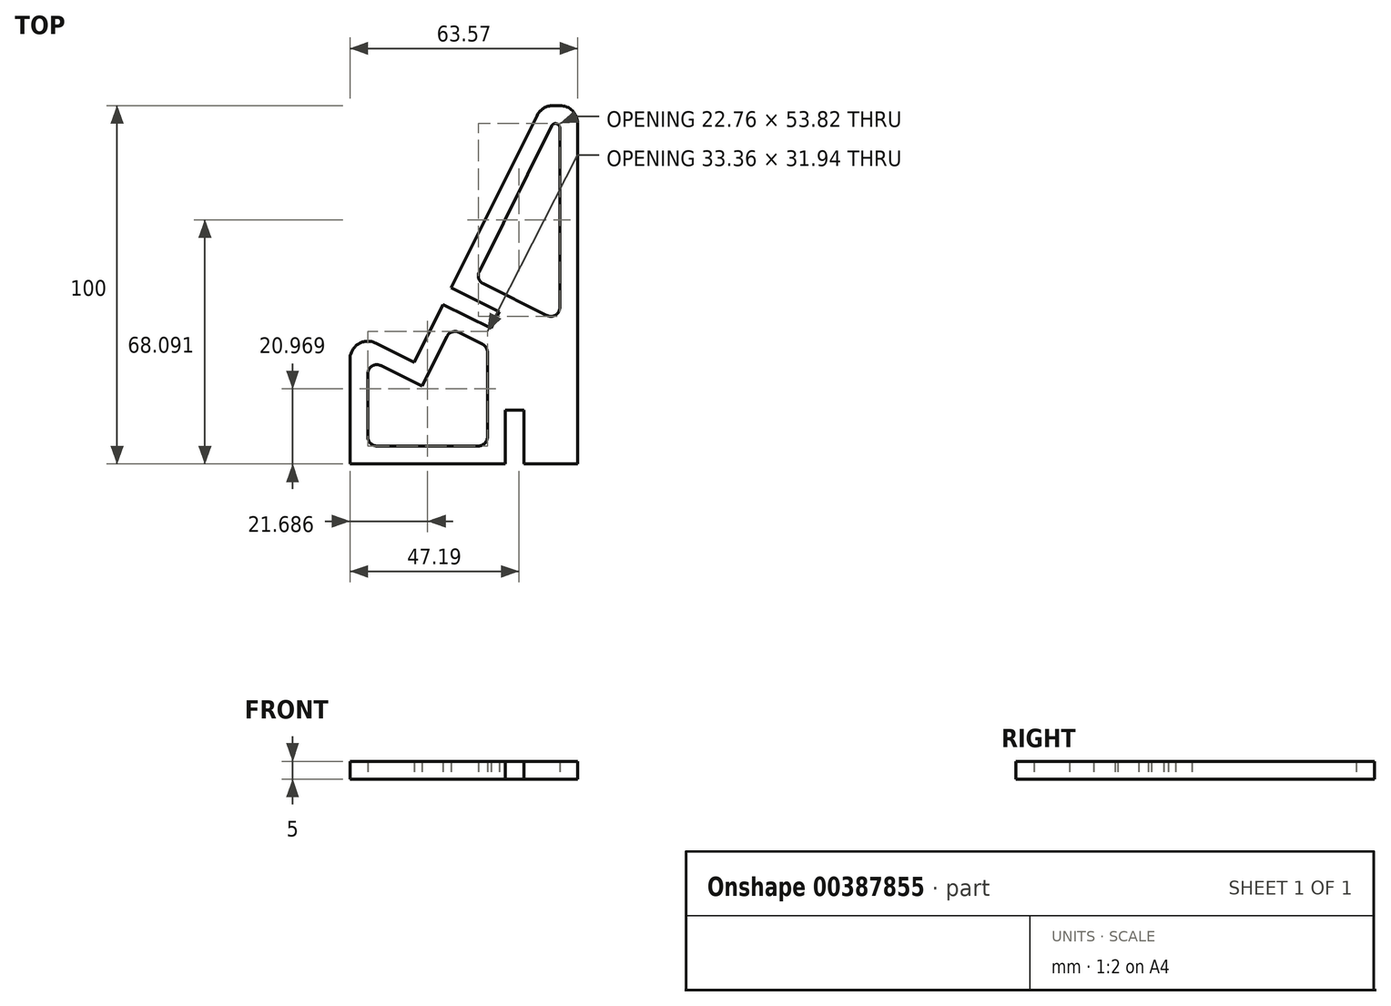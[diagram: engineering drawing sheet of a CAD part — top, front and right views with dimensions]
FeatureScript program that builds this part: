
annotation { "Feature Type Name" : "Feature", "Feature Type Description" : "" }
export const myFeature = defineFeature(function(context is Context, id is Id, definition is map)
    precondition{}
    {
        {
            var Q0;
            Q0=qCreatedBy(makeId("Top.planeOp"),FACE);
            var sketch = newSketch(context, id + "F0", { "sketchPlane" : qUnion([Q0])});
            skLineSegment(sketch, "E0", {"start": v(28.14, 25.7) * mm, "end": v(28.14, -69.3) * mm});
            skLineSegment(sketch, "E1", {"start": v(23.14, 30.7) * mm, "end": v(21.23, 30.7) * mm});
            skLineSegment(sketch, "E2", {"start": v(16.76, 27.94) * mm, "end": v(-7.18, -20.13) * mm});
            skLineSegment(sketch, "E3", {"start": v(-17.52, -40.9) * mm, "end": v(-28.2, -35.59) * mm});
            skLineSegment(sketch, "E4", {"start": v(-35.43, -40.06) * mm, "end": v(-35.43, -69.3) * mm});
            skLineSegment(sketch, "E5", {"start": v(7.94, -69.3) * mm, "end": v(7.94, -54.3) * mm});
            skLineSegment(sketch, "E6", {"start": v(7.94, -54.3) * mm, "end": v(13.14, -54.3) * mm});
            skLineSegment(sketch, "E7", {"start": v(13.14, -54.3) * mm, "end": v(13.14, -69.3) * mm});
            skLineSegment(sketch, "E8", {"start": v(-35.43, -69.3) * mm, "end": v(7.94, -69.3) * mm});
            skLineSegment(sketch, "E9", {"start": v(13.14, -69.3) * mm, "end": v(28.14, -69.3) * mm});
            skPoint(sketch, "E10.visualSharp", {"position": v(18.14, 30.7) * mm});
            skArc(sketch, "E10.filletArc", {"start": v(21.23, 30.7) * mm, "mid": v(18.6, 29.96) * mm, "end": v(16.76, 27.94) * mm});
            skPoint(sketch, "E11.visualSharp", {"position": v(28.14, 30.7) * mm});
            skArc(sketch, "E11.filletArc", {"start": v(28.14, 25.7) * mm, "mid": v(26.67, 29.25) * mm, "end": v(23.14, 30.7) * mm});
            skPoint(sketch, "E12.visualSharp", {"position": v(-35.43, -31.99) * mm});
            skArc(sketch, "E12.filletArc", {"start": v(-28.2, -35.59) * mm, "mid": v(-33.06, -35.81) * mm, "end": v(-35.43, -40.06) * mm});
            skLineSegment(sketch, "E13", {"start": v(-7.18, -20.13) * mm, "end": v(6.25, -26.82) * mm});
            skLineSegment(sketch, "E14", {"start": v(6.25, -26.82) * mm, "end": v(3.93, -31.48) * mm});
            skLineSegment(sketch, "E15", {"start": v(3.93, -31.48) * mm, "end": v(-9.5, -24.79) * mm});
            skLineSegment(sketch, "E16.trimOffspring", {"start": v(-9.5, -24.79) * mm, "end": v(-17.52, -40.9) * mm});
            skLineSegment(sketch, "E17.0", {"start": v(21.94, 25.7) * mm, "end": v(21.91, 25.7) * mm});
            skLineSegment(sketch, "E17.1", {"start": v(20.93, 25.1) * mm, "end": v(0.64, -15.65) * mm});
            skLineSegment(sketch, "E17.2", {"start": v(1.76, -19) * mm, "end": v(12.95, -24.57) * mm});
            skLineSegment(sketch, "E17.3", {"start": v(2.94, -61.8) * mm, "end": v(2.94, -49.3) * mm});
            skLineSegment(sketch, "E17.7", {"start": v(-27.93, -64.3) * mm, "end": v(0.44, -64.3) * mm});
            skLineSegment(sketch, "E17.8", {"start": v(-30.43, -44.1) * mm, "end": v(-30.43, -61.8) * mm});
            skLineSegment(sketch, "E17.9", {"start": v(-15.28, -47.6) * mm, "end": v(-26.81, -41.86) * mm});
            skLineSegment(sketch, "E17.10", {"start": v(23.14, 24.5) * mm, "end": v(23.14, -25.61) * mm});
            skLineSegment(sketch, "E17.11", {"start": v(-8.37, -33.73) * mm, "end": v(-15.28, -47.6) * mm});
            skLineSegment(sketch, "E17.12", {"start": v(1.55, -35.88) * mm, "end": v(-5.02, -32.6) * mm});
            skLineSegment(sketch, "E18", {"start": v(12.95, -24.57) * mm, "end": v(19.52, -27.85) * mm});
            skLineSegment(sketch, "E19", {"start": v(2.94, -49.3) * mm, "end": v(2.94, -38.12) * mm});
            skPoint(sketch, "E20.visualSharp", {"position": v(23.14, -29.65) * mm});
            skArc(sketch, "E20.filletArc", {"start": v(19.52, -27.85) * mm, "mid": v(21.95, -27.74) * mm, "end": v(23.14, -25.61) * mm});
            skPoint(sketch, "E21.visualSharp", {"position": v(-0.48, -17.89) * mm});
            skArc(sketch, "E21.filletArc", {"start": v(0.64, -15.65) * mm, "mid": v(0.5, -17.56) * mm, "end": v(1.76, -19) * mm});
            skPoint(sketch, "E22.visualSharp", {"position": v(2.94, -36.57) * mm});
            skArc(sketch, "E22.filletArc", {"start": v(2.94, -38.12) * mm, "mid": v(2.56, -36.8) * mm, "end": v(1.55, -35.88) * mm});
            skPoint(sketch, "E23.visualSharp", {"position": v(-7.25, -31.5) * mm});
            skArc(sketch, "E23.filletArc", {"start": v(-5.02, -32.6) * mm, "mid": v(-6.92, -32.48) * mm, "end": v(-8.37, -33.73) * mm});
            skPoint(sketch, "E24.visualSharp", {"position": v(-15.28, -47.6) * mm});
            skLineSegment(sketch, "E24.filletArc", {"start": v(-15.28, -47.6) * mm, "end": v(-15.28, -47.6) * mm});
            skPoint(sketch, "E25.visualSharp", {"position": v(-30.43, -64.3) * mm});
            skArc(sketch, "E25.filletArc", {"start": v(-30.43, -61.8) * mm, "mid": v(-29.7, -63.56) * mm, "end": v(-27.93, -64.3) * mm});
            skPoint(sketch, "E26.visualSharp", {"position": v(2.94, -64.3) * mm});
            skArc(sketch, "E26.filletArc", {"start": v(0.44, -64.3) * mm, "mid": v(2.2, -63.56) * mm, "end": v(2.94, -61.8) * mm});
            skArc(sketch, "E27.filletArc", {"start": v(-26.81, -41.86) * mm, "mid": v(-29.24, -41.97) * mm, "end": v(-30.43, -44.1) * mm});
            skArc(sketch, "E28.filletArc", {"start": v(23.14, 24.5) * mm, "mid": v(22.79, 25.36) * mm, "end": v(21.94, 25.7) * mm});
            skArc(sketch, "E29.filletArc", {"start": v(21.91, 25.7) * mm, "mid": v(21.34, 25.54) * mm, "end": v(20.93, 25.1) * mm});
            skSolve(sketch);
        }
        {
            var Q0;
            Q0=qSketchRegion(id+"F0",true);
            extrude(context, id + "F1", {"entities" : qUnion([Q0]), "depth" : 5 * mm});
        }
    });
